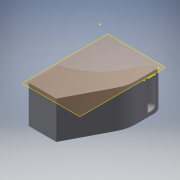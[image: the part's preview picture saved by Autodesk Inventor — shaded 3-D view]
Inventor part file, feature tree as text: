
AUTODESK INVENTOR PART (.ipt)
format: ipt  version: 2016 (Build 200138000, 138)  size: 230,912 bytes
history: native  units: mm
features: sketch x6, fillet x5, reference x5, extrude x3, plane x1, chamfer x1, shell x1, projected_geometry x1
ambient origin geometry x8: Origin, YZ Plane, XZ Plane, XY Plane, X Axis, Y Axis, Z Axis, Center Point
bodies: Solid1 (feature_tree)
feature tree (23):
  plane  "Work Plane1"
  extrude  "Extrusion1"  Depth=25.0mm TaperAngle=45.0deg
  chamfer  "Chamfer1"  Distance=2.0mm
  sketch  "Sketch2"  dims[d5=2.0mm]
  shell  "Shell1"  Thickness=3.0mm
  extrude  "Extrusion2"  Depth=2.0mm
  sketch  "Sketch4"  dims[d10=5.5mm d11=2.0mm d12=17.25mm d13=4.0mm d14=16.0mm d15=0.0mm]
  sketch  "Sketch5"
  fillet  "Fillet1"  Radius=17.25mm
  fillet  "Fillet2"  Radius=4.0mm
  fillet  "Fillet3"  Radius=16.0mm
  fillet  "Fillet4"  [1 undecoded]
  fillet  "Fillet5"  [1 undecoded]
  extrude  "Extrusion3"  [1 undecoded]
  sketch  "Sketch1"  dims[d0=20.0mm d1=0.0mm d2=25.0mm d3=13.0mm d4=45.0deg]
  sketch  "Sketch3"  dims[d6=8.0mm d7=2.0mm d8=0.0mm d9=3.0mm]
  reference  "Reference1"
  projected_geometry  "Projected Loop1"
  sketch  "Sketch6"
  reference  "Reference2"
  reference  "Reference3"
  reference  "Reference4"
  reference  "Reference5"
note: 3 required parameter values undecoded (feature->parameter linkage not recoverable at this tier; creation-order binding heuristic only, values carry confidence <= 0.55)
